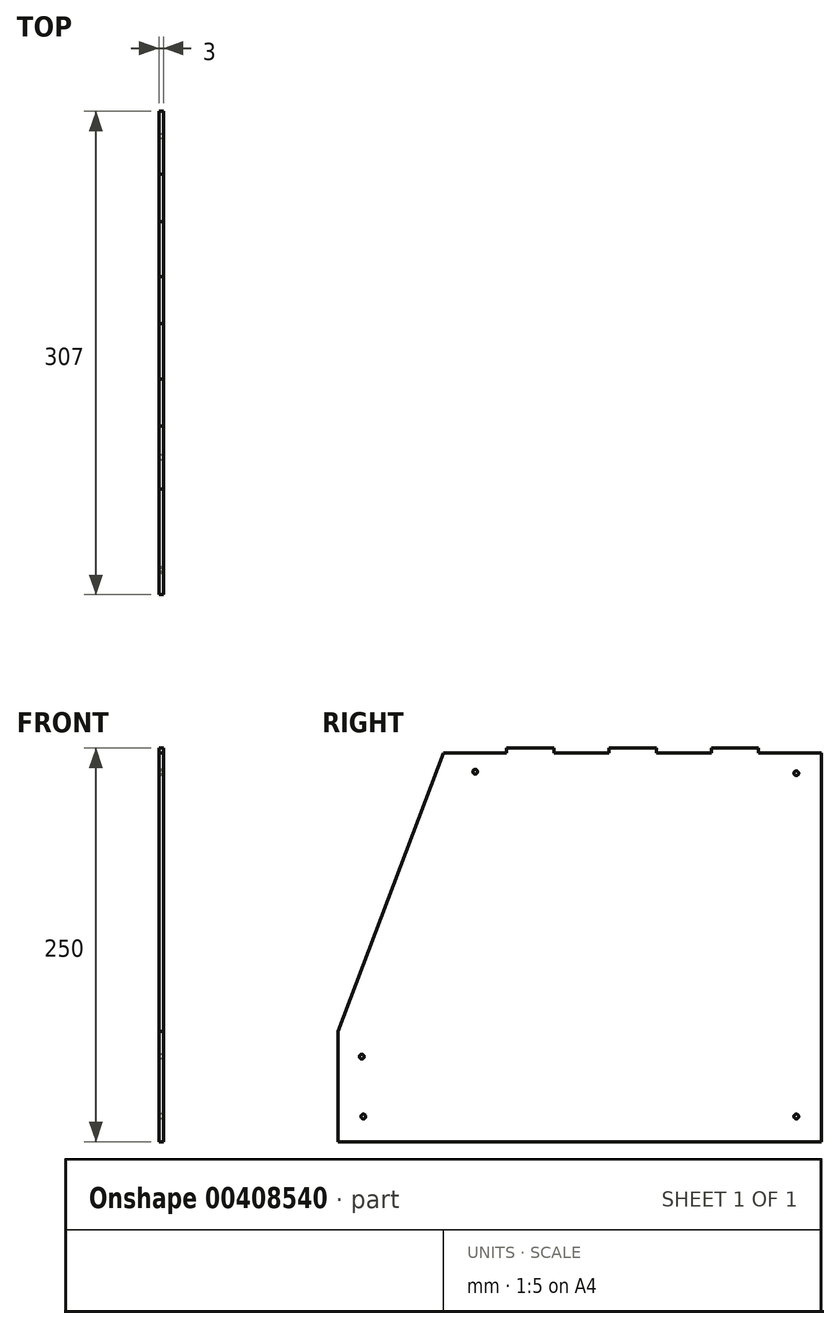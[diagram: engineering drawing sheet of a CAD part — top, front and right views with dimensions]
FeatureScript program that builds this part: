
annotation { "Feature Type Name" : "Feature", "Feature Type Description" : "" }
export const myFeature = defineFeature(function(context is Context, id is Id, definition is map)
    precondition{}
    {
        {
            var Q0;
            Q0=qCreatedBy(makeId("Right.planeOp"),FACE);
            var sketch = newSketch(context, id + "F0", { "sketchPlane" : qUnion([Q0])});
            skLineSegment(sketch, "E0.bottom", {"start": v(113.5, 125) * mm, "end": v(83.5, 125) * mm});
            skLineSegment(sketch, "E0.top", {"start": v(153.5, -125) * mm, "end": v(-153.5, -125) * mm});
            skLineSegment(sketch, "E0.left", {"start": v(153.5, 125) * mm, "end": v(153.5, -125) * mm});
            skLineSegment(sketch, "E0.right", {"start": v(-153.5, -55) * mm, "end": v(-153.5, -125) * mm});
            skPoint(sketch, "E0.middle", {"position": v(0, 0) * mm});
            skLineSegment(sketch, "E1", {"start": v(153.5, 122) * mm, "end": v(113.5, 122) * mm});
            skLineSegment(sketch, "E2", {"start": v(113.5, 122) * mm, "end": v(113.5, 125) * mm});
            skLineSegment(sketch, "E3", {"start": v(83.5, 125) * mm, "end": v(83.5, 122) * mm});
            skLineSegment(sketch, "E4", {"start": v(83.5, 122) * mm, "end": v(48.5, 122) * mm});
            skLineSegment(sketch, "E5", {"start": v(48.5, 122) * mm, "end": v(48.5, 125) * mm});
            skLineSegment(sketch, "E6", {"start": v(48.5, 125) * mm, "end": v(18.5, 125) * mm});
            skLineSegment(sketch, "E7", {"start": v(18.5, 125) * mm, "end": v(18.5, 122) * mm});
            skLineSegment(sketch, "E8", {"start": v(18.5, 122) * mm, "end": v(-16.5, 122) * mm});
            skLineSegment(sketch, "E9", {"start": v(-16.5, 122) * mm, "end": v(-16.5, 125) * mm});
            skLineSegment(sketch, "E10.trimOffspring", {"start": v(-16.5, 125) * mm, "end": v(-46.5, 125) * mm});
            skLineSegment(sketch, "E11", {"start": v(-46.5, 125) * mm, "end": v(-46.5, 122) * mm});
            skLineSegment(sketch, "E12", {"start": v(-46.5, 122) * mm, "end": v(-86.5, 122) * mm});
            skLineSegment(sketch, "E13", {"start": v(-86.5, 122) * mm, "end": v(-153.5, -55) * mm});
            skCircle(sketch, "E14", {"center": v(137.5, -109) * mm, "radius": 1.5 * mm});
            skCircle(sketch, "E15", {"center": v(137.5, 109) * mm, "radius": 1.5 * mm});
            skCircle(sketch, "E16", {"center": v(-66.5, 110) * mm, "radius": 1.5 * mm});
            skCircle(sketch, "E17", {"center": v(-137.5, -109) * mm, "radius": 1.5 * mm});
            skCircle(sketch, "E18", {"center": v(-138.5, -71) * mm, "radius": 1.5 * mm});
            skSolve(sketch);
        }
        {
            var Q0;
            {var subQ0=sQuery(id+"F0.wireOp",EDGE,"E0.top");Q0=makeQuery(id+"F0.imprint","IMPRINT",FACE,{"disambiguationData":[TD([[makeQuery(id+"F0.imprint","IMPRINT",EDGE,{"derivedFrom":subQ0}),-1.0]])]});}
            extrude(context, id + "F1", {"entities" : qUnion([Q0]), "depth" : 3 * mm});
        }
    });
